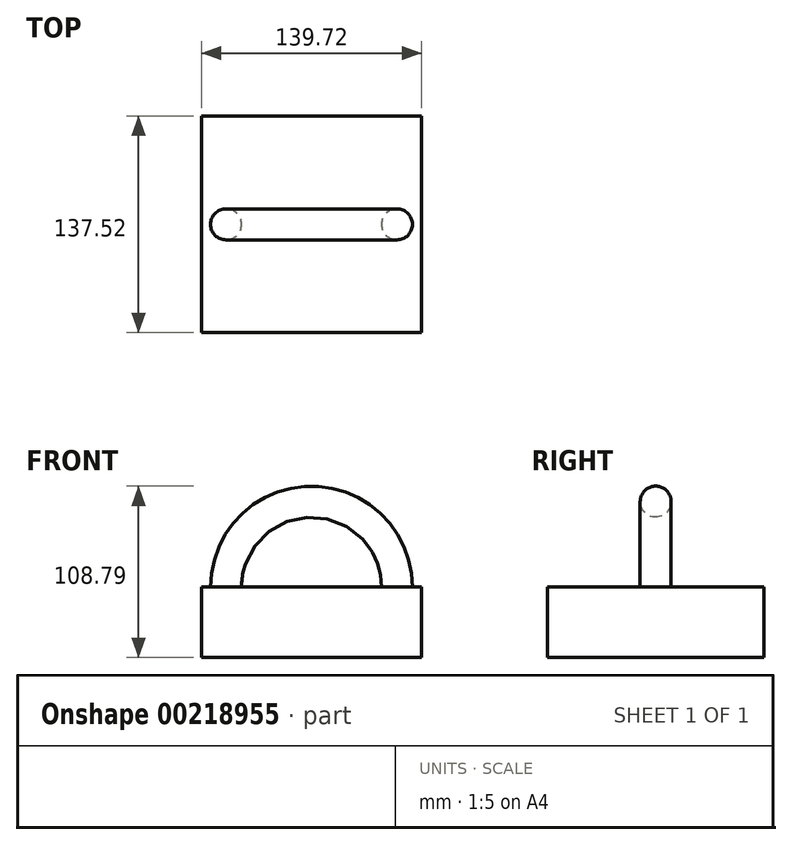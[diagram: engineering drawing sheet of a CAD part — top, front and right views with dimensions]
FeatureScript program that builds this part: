
annotation { "Feature Type Name" : "Feature", "Feature Type Description" : "" }
export const myFeature = defineFeature(function(context is Context, id is Id, definition is map)
    precondition{}
    {
        {
            var Q0;
            Q0=qCreatedBy(makeId("Top.planeOp"),FACE);
            var sketch = newSketch(context, id + "F0", { "sketchPlane" : qUnion([Q0])});
            skLineSegment(sketch, "E0.bottom", {"start": v(69.86, -68.76) * mm, "end": v(-69.86, -68.76) * mm});
            skLineSegment(sketch, "E0.top", {"start": v(69.86, 68.76) * mm, "end": v(-69.86, 68.76) * mm});
            skLineSegment(sketch, "E0.left", {"start": v(69.86, -68.76) * mm, "end": v(69.86, 68.76) * mm});
            skLineSegment(sketch, "E0.right", {"start": v(-69.86, -68.76) * mm, "end": v(-69.86, 68.76) * mm});
            skPoint(sketch, "E0.middle", {"position": v(0, 0) * mm});
            skLineSegment(sketch, "E1", {"start": v(0, 68.76) * mm, "end": v(0, -68.76) * mm});
            skSolve(sketch);
        }
        {
            var Q0;
            Q0=qCreatedBy(makeId("Top.planeOp"),FACE);
            var sketch = newSketch(context, id + "F1", { "sketchPlane" : qUnion([Q0])});
            skCircle(sketch, "E2", {"center": v(54.26, 0) * mm, "radius": 9.82 * mm});
            skSolve(sketch);
        }
        {
            var Q0;
            Q0 = qSketchRegion(id + "F0", true);
            extrude(context, id + "F2", {"entities" : qUnion([Q0]), "oppositeDirection" : true, "depth" : 44.7 * mm});
        }
        {
            var Q0;
            Q0 = qSketchRegion(id + "F1", true);
            var Q1;
            Q1=sQuery(id+"F0.wireOp",EDGE,"E1");
            revolve(context, id + "F3", {"operationType" : NewBodyOperationType.ADD, "entities" : qUnion([Q0]), "axis" : qUnion([Q1]), "revolveType" : RevolveType.ONE_DIRECTION, "angle" : 180 * degree});
        }
    });
